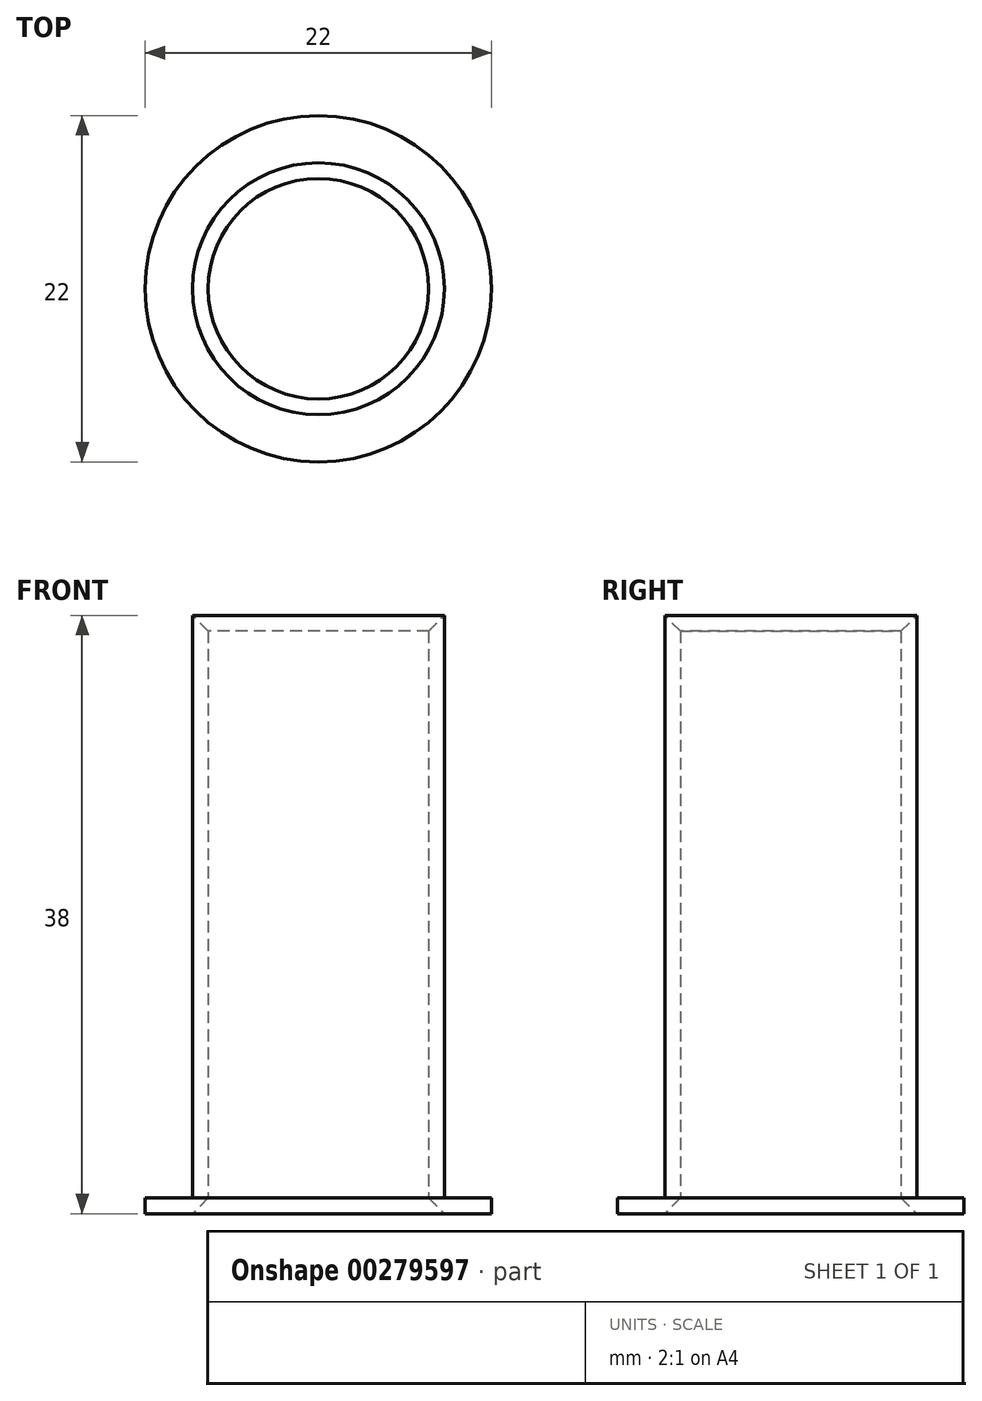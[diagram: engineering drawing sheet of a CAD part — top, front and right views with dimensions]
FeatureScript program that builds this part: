
annotation { "Feature Type Name" : "Feature", "Feature Type Description" : "" }
export const myFeature = defineFeature(function(context is Context, id is Id, definition is map)
    precondition{}
    {
        {
            var Q0;
            Q0=qCreatedBy(makeId("Top.planeOp"),FACE);
            var sketch = newSketch(context, id + "F0", { "sketchPlane" : qUnion([Q0])});
            skCircle(sketch, "E0", {"center": v(0, 0) * mm, "radius": 7 * mm});
            skCircle(sketch, "E1", {"center": v(0, 0) * mm, "radius": 8 * mm});
            skCircle(sketch, "E2", {"center": v(0, 0) * mm, "radius": 11 * mm});
            skSolve(sketch);
        }
        {
            var Q0;
            Q0=makeQuery(id+"F0.imprint","IMPRINT",FACE,{"disambiguationData":[TD([[makeQuery(id+"F0.imprint","IMPRINT",EDGE,{"derivedFrom":sQuery(id+"F0.wireOp",EDGE,"E1")}),-1.0]])]});
            extrude(context, id + "F1", {"entities" : qUnion([Q0]), "depth" : 1 * mm});
        }
        {
            var Q0;
            Q0=makeQuery(id+"F0.imprint","IMPRINT",FACE,{"disambiguationData":[TD([[makeQuery(id+"F0.imprint","IMPRINT",EDGE,{"derivedFrom":sQuery(id+"F0.wireOp",EDGE,"E0")}),-1.0]])]});
            extrude(context, id + "F2", {"entities" : qUnion([Q0]), "operationType" : NewBodyOperationType.ADD, "depth" : 39 * mm});
        }
        {
            var Q0;
            Q0=makeQuery(id+"F1.opExtrude","CAP_EDGE",EDGE,{"disambiguationData":[OSD([sQuery(id+"F0.wireOp",EDGE,"E1")])],"isStart":false});
            var Q1;
            Q1=makeQuery(id+"F2.opExtrude","CAP_EDGE",EDGE,{"disambiguationData":[OSD([sQuery(id+"F0.wireOp",EDGE,"E0")])],"isStart":true});
            chamfer(context, id + "F3", {"entities" : qUnion([Q0, Q1]), "width" : 1 * mm, "tangentPropagation" : true});
        }
        {
            var Q0;
            Q0=makeQuery(id+"F2.opExtrude","CAP_EDGE",EDGE,{"disambiguationData":[OSD([sQuery(id+"F0.wireOp",EDGE,"E0")])],"isStart":false});
            chamfer(context, id + "F4", {"entities" : qUnion([Q0]), "width" : 2 * mm, "tangentPropagation" : true});
        }
    });
